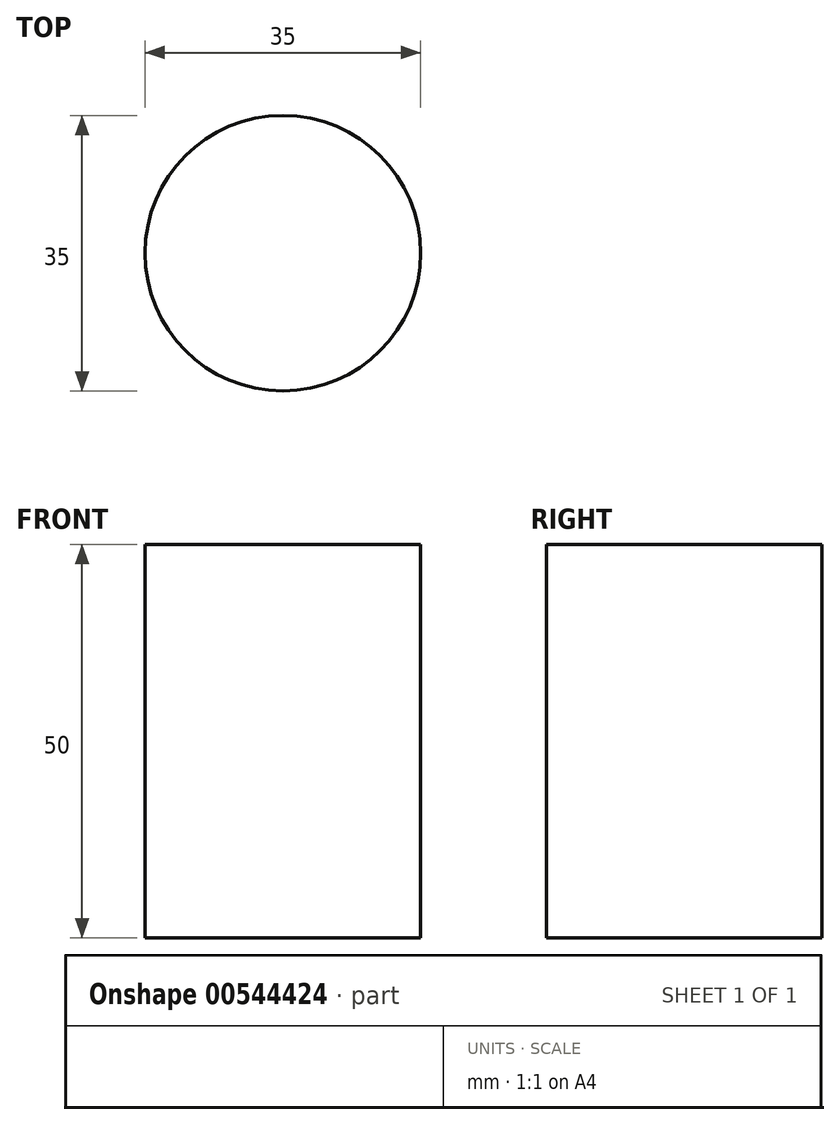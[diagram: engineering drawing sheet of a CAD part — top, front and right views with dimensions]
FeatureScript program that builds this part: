
annotation { "Feature Type Name" : "Feature", "Feature Type Description" : "" }
export const myFeature = defineFeature(function(context is Context, id is Id, definition is map)
    precondition{}
    {
        {
            var Q0;
            Q0=qCreatedBy(makeId("Top.planeOp"),FACE);
            var sketch = newSketch(context, id + "F0", { "sketchPlane" : qUnion([Q0])});
            skCircle(sketch, "E0", {"center": v(0, 0) * mm, "radius": 17.5 * mm});
            skSolve(sketch);
        }
        {
            var Q0;
            Q0 = qSketchRegion(id + "F0", true);
            extrude(context, id + "F1", {"entities" : qUnion([Q0]), "depth" : 50 * mm, "offsetDistance" : 25 * mm});
        }
    });
